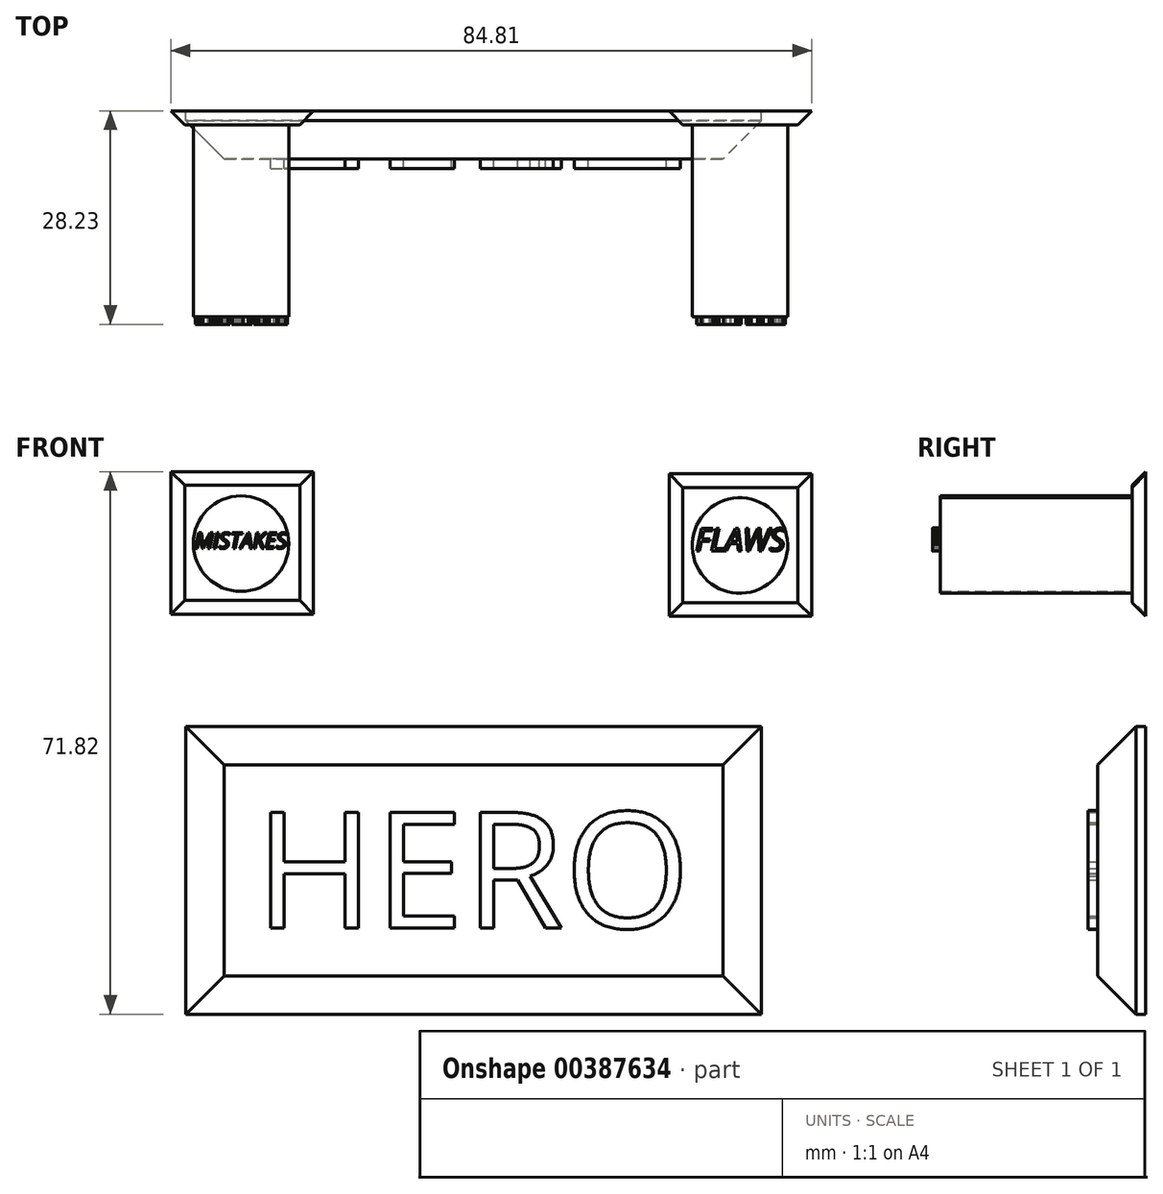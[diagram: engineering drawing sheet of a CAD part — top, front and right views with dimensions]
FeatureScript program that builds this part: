
annotation { "Feature Type Name" : "Feature", "Feature Type Description" : "" }
export const myFeature = defineFeature(function(context is Context, id is Id, definition is map)
    precondition{}
    {
        {
            var Q0;
            Q0=qCreatedBy(makeId("Front.planeOp"),FACE);
            var sketch = newSketch(context, id + "F0", { "sketchPlane" : qUnion([Q0])});
            skLineSegment(sketch, "E0.bottom", {"start": v(-108.34, 31.43) * mm, "end": v(-82.94, 31.43) * mm});
            skLineSegment(sketch, "E0.top", {"start": v(-108.34, 6.03) * mm, "end": v(-82.94, 6.03) * mm});
            skLineSegment(sketch, "E0.left", {"start": v(-108.34, 31.43) * mm, "end": v(-108.34, 6.03) * mm});
            skLineSegment(sketch, "E0.right", {"start": v(-82.94, 31.43) * mm, "end": v(-82.94, 6.03) * mm});
            skLineSegment(sketch, "E1.bottom", {"start": v(-42.4, 31.13) * mm, "end": v(-17, 31.13) * mm});
            skLineSegment(sketch, "E1.top", {"start": v(-42.4, 5.73) * mm, "end": v(-17, 5.73) * mm});
            skLineSegment(sketch, "E1.left", {"start": v(-42.4, 31.13) * mm, "end": v(-42.4, 5.73) * mm});
            skLineSegment(sketch, "E1.right", {"start": v(-17, 31.13) * mm, "end": v(-17, 5.73) * mm});
            skSolve(sketch);
        }
        {
            var Q0;
            Q0=makeQuery(id+"F0.imprint","IMPRINT",FACE,{"disambiguationData":[TD([[makeQuery(id+"F0.imprint","IMPRINT",EDGE,{"derivedFrom":sQuery(id+"F0.wireOp",EDGE,"E0.bottom")}),-1.0]])]});
            var Q1;
            Q1=makeQuery(id+"F0.imprint","IMPRINT",FACE,{"disambiguationData":[TD([[makeQuery(id+"F0.imprint","IMPRINT",EDGE,{"derivedFrom":sQuery(id+"F0.wireOp",EDGE,"E1.bottom")}),-1.0]])]});
            extrude(context, id + "F1", {"entities" : qUnion([Q0, Q1]), "depth" : 1.81 * mm});
        }
        {
            var Q0;
            Q0=makeQuery(id+"F1.opExtrude","CAP_FACE",FACE,{"disambiguationData":[OSD([sQuery(id+"F0.wireOp",EDGE,"E0.bottom"),sQuery(id+"F0.wireOp",EDGE,"E0.top"),sQuery(id+"F0.wireOp",EDGE,"E0.left"),sQuery(id+"F0.wireOp",EDGE,"E0.right")])],"isStart":false});
            var Q1;
            Q1=makeQuery(id+"F1.opExtrude","CAP_FACE",FACE,{"disambiguationData":[OSD([sQuery(id+"F0.wireOp",EDGE,"E1.bottom"),sQuery(id+"F0.wireOp",EDGE,"E1.top"),sQuery(id+"F0.wireOp",EDGE,"E1.left"),sQuery(id+"F0.wireOp",EDGE,"E1.right")])],"isStart":false});
            chamfer(context, id + "F2", {"entities" : qUnion([Q0, Q1]), "width" : 5.08 * mm, "tangentPropagation" : true});
        }
        {
            var Q0;
            Q0=makeQuery(id+"F1.opExtrude","CAP_FACE",FACE,{"disambiguationData":[OSD([sQuery(id+"F0.wireOp",EDGE,"E0.bottom"),sQuery(id+"F0.wireOp",EDGE,"E0.top"),sQuery(id+"F0.wireOp",EDGE,"E0.left"),sQuery(id+"F0.wireOp",EDGE,"E0.right")])],"isStart":false});
            var sketch = newSketch(context, id + "F3", { "sketchPlane" : qUnion([Q0])});
            skCircle(sketch, "E2", {"center": v(-95.8, 18.63) * mm, "radius": 6.32 * mm});
            skCircle(sketch, "E3", {"center": v(-29.76, 18.37) * mm, "radius": 6.32 * mm});
            skSolve(sketch);
        }
        {
            var Q0;
            Q0 = qSketchRegion(id + "F3", true);
            extrude(context, id + "F4", {"entities" : qUnion([Q0]), "operationType" : NewBodyOperationType.ADD, "depth" : 25.4 * mm});
        }
        {
            var Q0;
            Q0=makeQuery(id+"F4.opExtrude","CAP_FACE",FACE,{"disambiguationData":[OSD([sQuery(id+"F3.wireOp",EDGE,"E2")])],"isStart":false});
            var sketch = newSketch(context, id + "F5", { "sketchPlane" : qUnion([Q0])});
            skText(sketch, "E4", { "text": "MISTAKES", "fontName": "OpenSans-Italic.ttf"});
            const initialGuessF5  = {"E4": [-0.10195, 0.01801, 1, 0, 0.00208]};
            skSetInitialGuess(sketch, initialGuessF5);
            skSolve(sketch);
        }
        {
            var Q0;
            Q0=makeQuery(id+"F4.opExtrude","CAP_FACE",FACE,{"disambiguationData":[OSD([sQuery(id+"F3.wireOp",EDGE,"E3")])],"isStart":false});
            var sketch = newSketch(context, id + "F6", { "sketchPlane" : qUnion([Q0])});
            skText(sketch, "E5", { "text": "FLAWS", "fontName": "OpenSans-Italic.ttf"});
            const initialGuessF6  = {"E5": [-0.03565, 0.01768, 1, 0, 0.00299]};
            skSetInitialGuess(sketch, initialGuessF6);
            skSolve(sketch);
        }
        {
            var Q0;
            Q0 = qSketchRegion(id + "F5", true);
            var Q1;
            Q1 = qSketchRegion(id + "F6", true);
            extrude(context, id + "F7", {"entities" : qUnion([Q0, Q1]), "operationType" : NewBodyOperationType.ADD, "depth" : 1.02 * mm});
        }
        {
            var Q0;
            Q0=qCreatedBy(makeId("Front.planeOp"),FACE);
            var sketch = newSketch(context, id + "F8", { "sketchPlane" : qUnion([Q0])});
            skLineSegment(sketch, "E6.bottom", {"start": v(-103.12, -5.55) * mm, "end": v(-26.92, -5.55) * mm});
            skLineSegment(sketch, "E6.top", {"start": v(-103.12, -43.65) * mm, "end": v(-26.92, -43.65) * mm});
            skLineSegment(sketch, "E6.left", {"start": v(-103.12, -5.55) * mm, "end": v(-103.12, -43.65) * mm});
            skLineSegment(sketch, "E6.right", {"start": v(-26.92, -5.55) * mm, "end": v(-26.92, -43.65) * mm});
            skSolve(sketch);
        }
        {
            var Q0;
            Q0 = qSketchRegion(id + "F8", true);
            extrude(context, id + "F9", {"entities" : qUnion([Q0]), "depth" : 6.35 * mm});
        }
        {
            var Q0;
            Q0=makeQuery(id+"F9.opExtrude","CAP_FACE",FACE,{"disambiguationData":[OSD([sQuery(id+"F8.wireOp",EDGE,"E6.bottom"),sQuery(id+"F8.wireOp",EDGE,"E6.top"),sQuery(id+"F8.wireOp",EDGE,"E6.left"),sQuery(id+"F8.wireOp",EDGE,"E6.right")])],"isStart":false});
            chamfer(context, id + "F10", {"entities" : qUnion([Q0]), "width" : 5.08 * mm, "tangentPropagation" : true});
        }
        {
            var Q0;
            Q0=makeQuery(id+"F9.opExtrude","CAP_FACE",FACE,{"disambiguationData":[OSD([sQuery(id+"F8.wireOp",EDGE,"E6.bottom"),sQuery(id+"F8.wireOp",EDGE,"E6.top"),sQuery(id+"F8.wireOp",EDGE,"E6.left"),sQuery(id+"F8.wireOp",EDGE,"E6.right")])],"isStart":false});
            var sketch = newSketch(context, id + "F11", { "sketchPlane" : qUnion([Q0])});
            skText(sketch, "E7", { "text": "HERO", "fontName": "OpenSans-Regular.ttf"});
            const initialGuessF11  = {"E7": [-0.09399, -0.03225, 1, 0, 0.01543]};
            skSetInitialGuess(sketch, initialGuessF11);
            skSolve(sketch);
        }
        {
            var Q0;
            Q0 = qSketchRegion(id + "F11", true);
            extrude(context, id + "F12", {"entities" : qUnion([Q0]), "operationType" : NewBodyOperationType.ADD, "depth" : 1.27 * mm});
        }
    });
